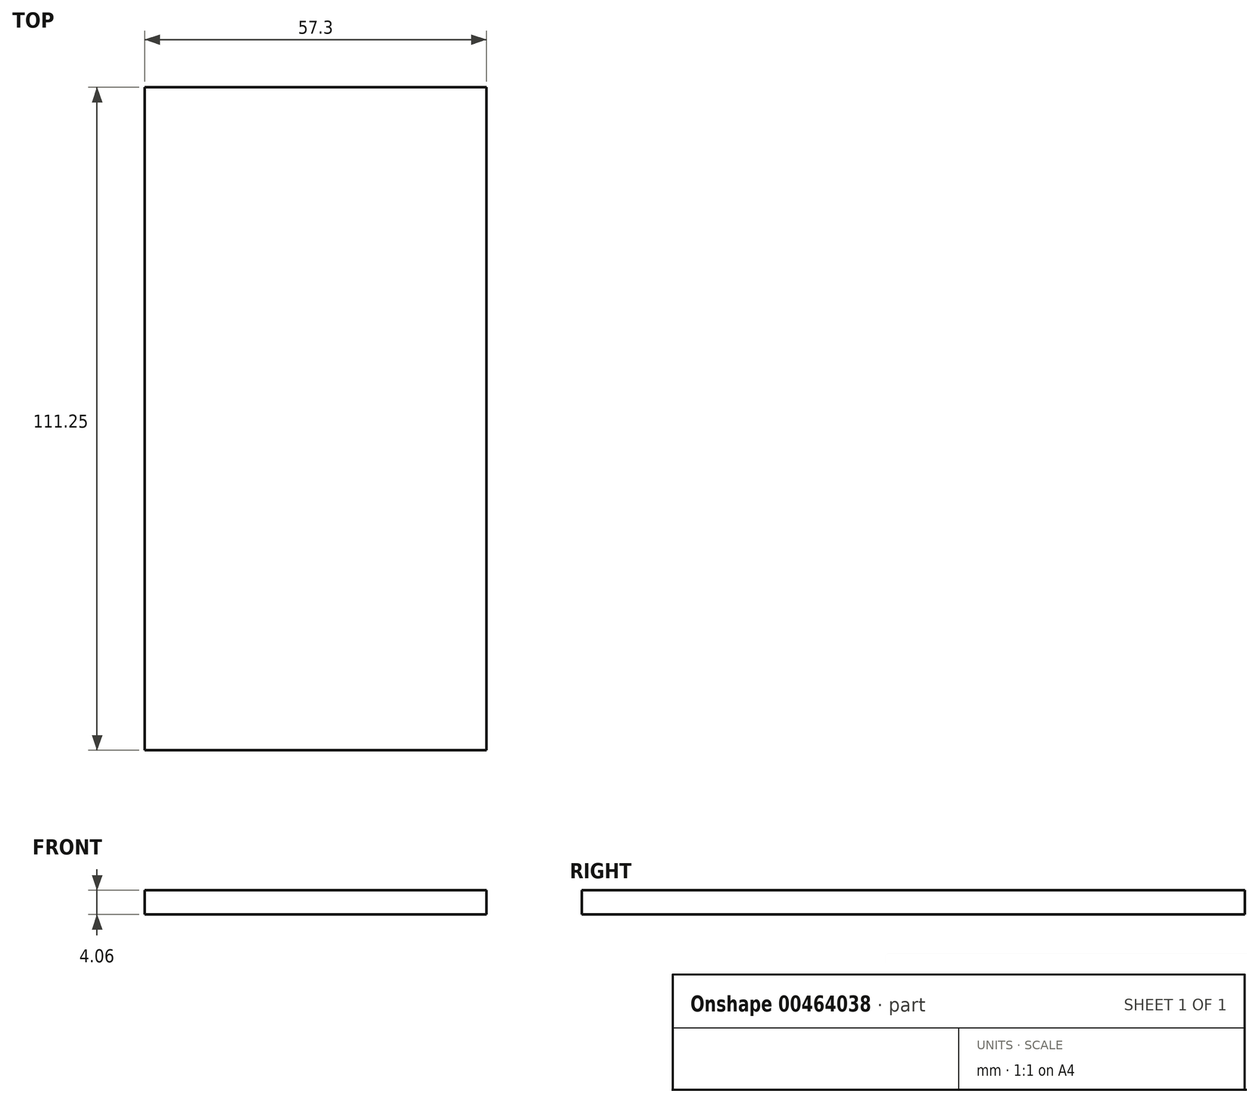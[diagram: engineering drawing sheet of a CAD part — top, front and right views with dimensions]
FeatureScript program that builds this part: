
annotation { "Feature Type Name" : "Feature", "Feature Type Description" : "" }
export const myFeature = defineFeature(function(context is Context, id is Id, definition is map)
    precondition{}
    {
        {
            var Q0;
            Q0=qCreatedBy(makeId("Top.planeOp"),FACE);
            var sketch = newSketch(context, id + "F0", { "sketchPlane" : qUnion([Q0])});
            skLineSegment(sketch, "E0.bottom", {"start": v(-57.3, 58.67) * mm, "end": v(0, 58.67) * mm});
            skLineSegment(sketch, "E0.top", {"start": v(-57.3, -52.58) * mm, "end": v(0, -52.58) * mm});
            skLineSegment(sketch, "E0.left", {"start": v(-57.3, 58.67) * mm, "end": v(-57.3, -52.58) * mm});
            skLineSegment(sketch, "E0.right", {"start": v(0, 58.67) * mm, "end": v(0, -52.58) * mm});
            skSolve(sketch);
        }
        {
            var Q0;
            Q0=makeQuery(id+"F0.imprint","IMPRINT",FACE,{"disambiguationData":[TD([[makeQuery(id+"F0.imprint","IMPRINT",EDGE,{"derivedFrom":sQuery(id+"F0.wireOp",EDGE,"E0.bottom")}),-1.0]])]});
            extrude(context, id + "F1", {"entities" : qUnion([Q0]), "depth" : 4.06 * mm});
        }
    });
